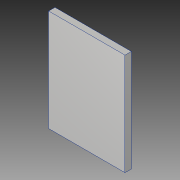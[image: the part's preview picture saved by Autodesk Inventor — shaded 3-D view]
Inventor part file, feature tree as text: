
AUTODESK INVENTOR PART (.ipt)
format: ipt  version: 2019 (Build 230136000, 136)  size: 82,944 bytes
history: native  units: in
note: dims shown in document units (in); Inventor stores cm internally (conversion verified against a paired STEP export)
features: extrude x1, sketch x1
ambient origin geometry x8: Origin, YZ Plane, XZ Plane, XY Plane, X Axis, Y Axis, Z Axis, Center Point
bodies: Solid1 (feature_tree)
feature tree (2):
  extrude  "Extrusion1"  [1 undecoded]
  sketch  "Sketch1"  dims[d3=0.0in]
note: 1 required parameter value undecoded (feature->parameter linkage not recoverable at this tier; creation-order binding heuristic only, values carry confidence <= 0.55)
